# Revit family: Valve_Rough-Thermostatic-DXV-D3500552X_Series
name_source: partatom
category: Plumbing Fixtures
units: mm (PartAtom-declared; Revit-internal decimal feet)

## family parameters
Cut with Voids When Loaded = No
Host = Face
OmniClass Number = 23.45.05.14.17
OmniClass Title = Showers
Part Type = Normal
Room Calculation Point = No
Round Connector Dimension = Use Radius
Shared = Yes

## types (2) — shared parameters
Assembly Code = D2010710
Back to Finished Wall = 3"
Back to Finished Wall Constraint = 3"
CW Connection = Yes
CWFU = 2
Default Elevation = 0"
Description = 2-HANDLE THERMOSTATIC ROUGH VALVE WITH 2-WAY DIVERTER - DISCRETE FUNCTION
Finish = Metal-DXV-Brass
HW Connection = Yes
HWFU = 3
Height = 3 3/8"
Hot/Cold Water Connection to Wall Constraint = 3 11/16"
Hydronic Supply Diameter = 1/2"
Hydronic Supply Radius = 1/4"
Hydronic Supply Width = 1 11/16"
IAPMO Compliance = Meets or Exceeds ASME A112.18.1/CSA B125.1/ASSE 1016
Installation Type = Wall Mounted
Length = 1 3/4"
Manufacturer = DXV
Material = Metal-DXV-Brass
Price = Prices may vary. Please consult Manufacturer Representative for most up-to-date price list.
Product Documentation Link = https://dxv01.blob.core.windows.net
Product Page URL = https://www.dxv.com
URL = www.dxv.com
Vent Connection = No
WFU = 4
Waste Connection = No
Width = 5 7/8"

## per-type parameters (varying)
| type | CEC Compliant | CalGreen Compliant | Hot/Cold Water Connection to Wall | Type Comments |
| D35005522.191 | Yes | Yes | 3 11/16" | Discrete Functions |
| D35005522S.191 | No | No | 0" | Shared Functions |

note: column(s) folded — value = type name in every type: Model

## geometry (parser evidence)
native form markers: Sweep x3
no freeform markers — native parametric forms only
